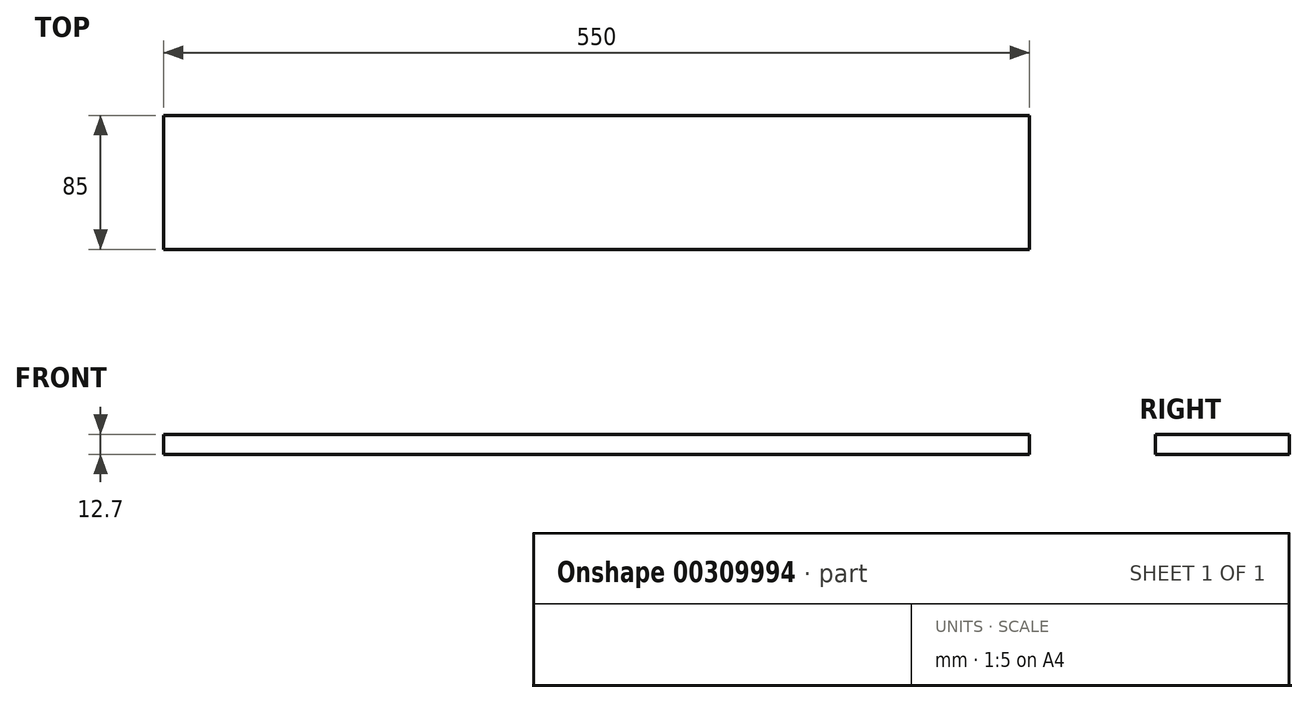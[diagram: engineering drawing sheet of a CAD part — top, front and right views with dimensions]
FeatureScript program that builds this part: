
annotation { "Feature Type Name" : "Feature", "Feature Type Description" : "" }
export const myFeature = defineFeature(function(context is Context, id is Id, definition is map)
    precondition{}
    {
        {
            var Q0;
            Q0=qCreatedBy(makeId("Top.planeOp"),FACE);
            var sketch = newSketch(context, id + "F0", { "sketchPlane" : qUnion([Q0])});
            skLineSegment(sketch, "E0.bottom", {"start": v(-275, 42.5) * mm, "end": v(275, 42.5) * mm});
            skLineSegment(sketch, "E0.top", {"start": v(-275, -42.5) * mm, "end": v(275, -42.5) * mm});
            skLineSegment(sketch, "E0.left", {"start": v(-275, 42.5) * mm, "end": v(-275, -42.5) * mm});
            skLineSegment(sketch, "E0.right", {"start": v(275, 42.5) * mm, "end": v(275, -42.5) * mm});
            skLineSegment(sketch, "E1", {"start": v(-275, 42.5) * mm, "end": v(275, -42.5) * mm, "construction": true});
            skSolve(sketch);
        }
        {
            var Q0;
            Q0=qSketchRegion(id+"F0",true);
            extrude(context, id + "F1", {"entities" : qUnion([Q0]), "depth" : 12.7 * mm});
        }
    });
